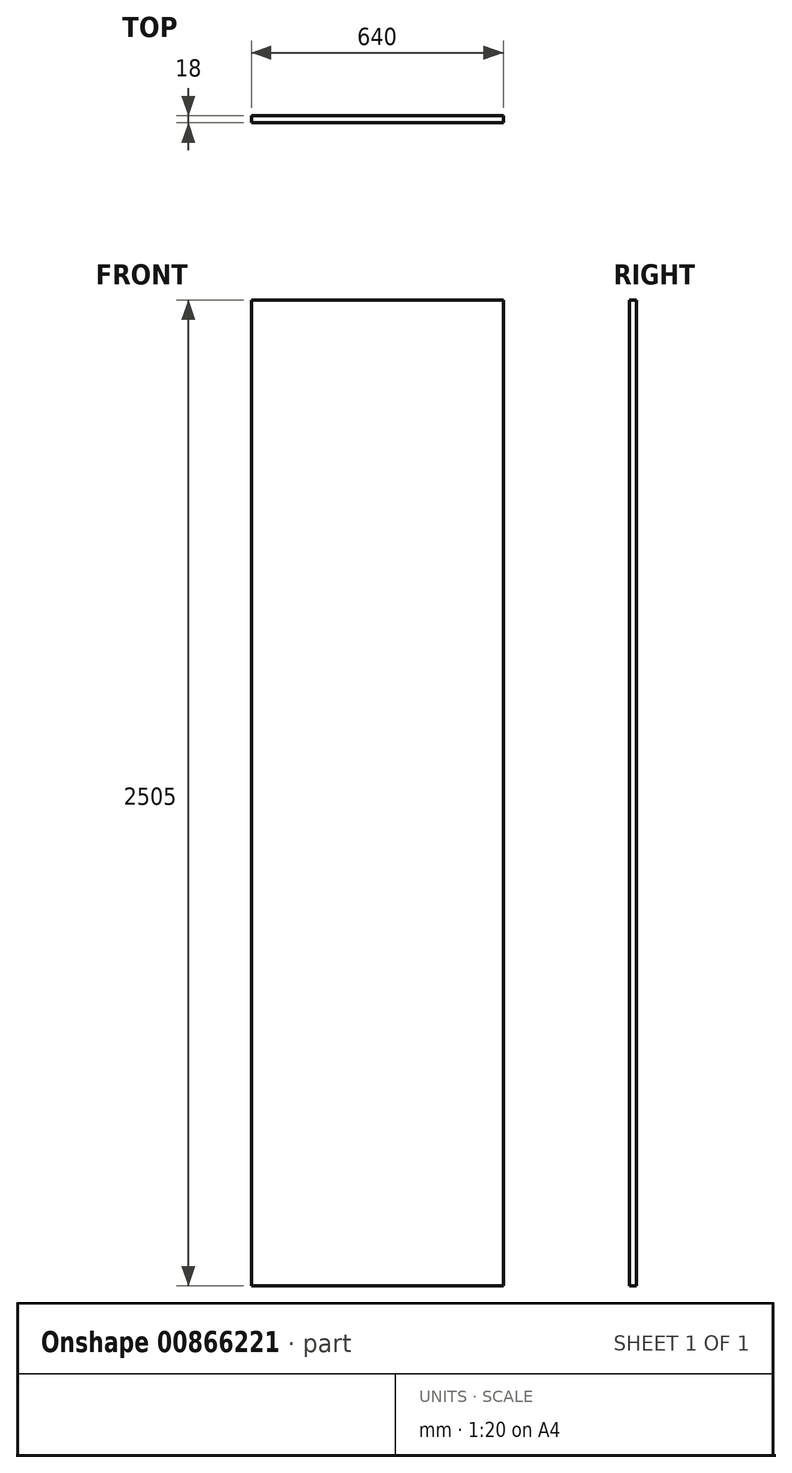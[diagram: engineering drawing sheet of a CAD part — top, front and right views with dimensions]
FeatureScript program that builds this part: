
annotation { "Feature Type Name" : "Feature", "Feature Type Description" : "" }
export const myFeature = defineFeature(function(context is Context, id is Id, definition is map)
    precondition{}
    {
        {
            var Q0;
            Q0=qCreatedBy(makeId("Top.planeOp"),FACE);
            var sketch = newSketch(context, id + "F0", { "sketchPlane" : qUnion([Q0])});
            skLineSegment(sketch, "E0.bottom", {"start": v(320, 9) * mm, "end": v(-320, 9) * mm});
            skLineSegment(sketch, "E0.top", {"start": v(320, -9) * mm, "end": v(-320, -9) * mm});
            skLineSegment(sketch, "E0.left", {"start": v(320, 9) * mm, "end": v(320, -9) * mm});
            skLineSegment(sketch, "E0.right", {"start": v(-320, 9) * mm, "end": v(-320, -9) * mm});
            skPoint(sketch, "E0.middle", {"position": v(0, 0) * mm});
            skSolve(sketch);
        }
        {
            var Q0;
            Q0=makeQuery(id+"F0.imprint","IMPRINT",FACE,{"disambiguationData":[TD([[makeQuery(id+"F0.imprint","IMPRINT",EDGE,{"derivedFrom":sQuery(id+"F0.wireOp",EDGE,"E0.bottom")}),1.0]])]});
            extrude(context, id + "F1", {"entities" : qUnion([Q0]), "depth" : 2505 * mm, "offsetDistance" : 25 * mm});
        }
    });
